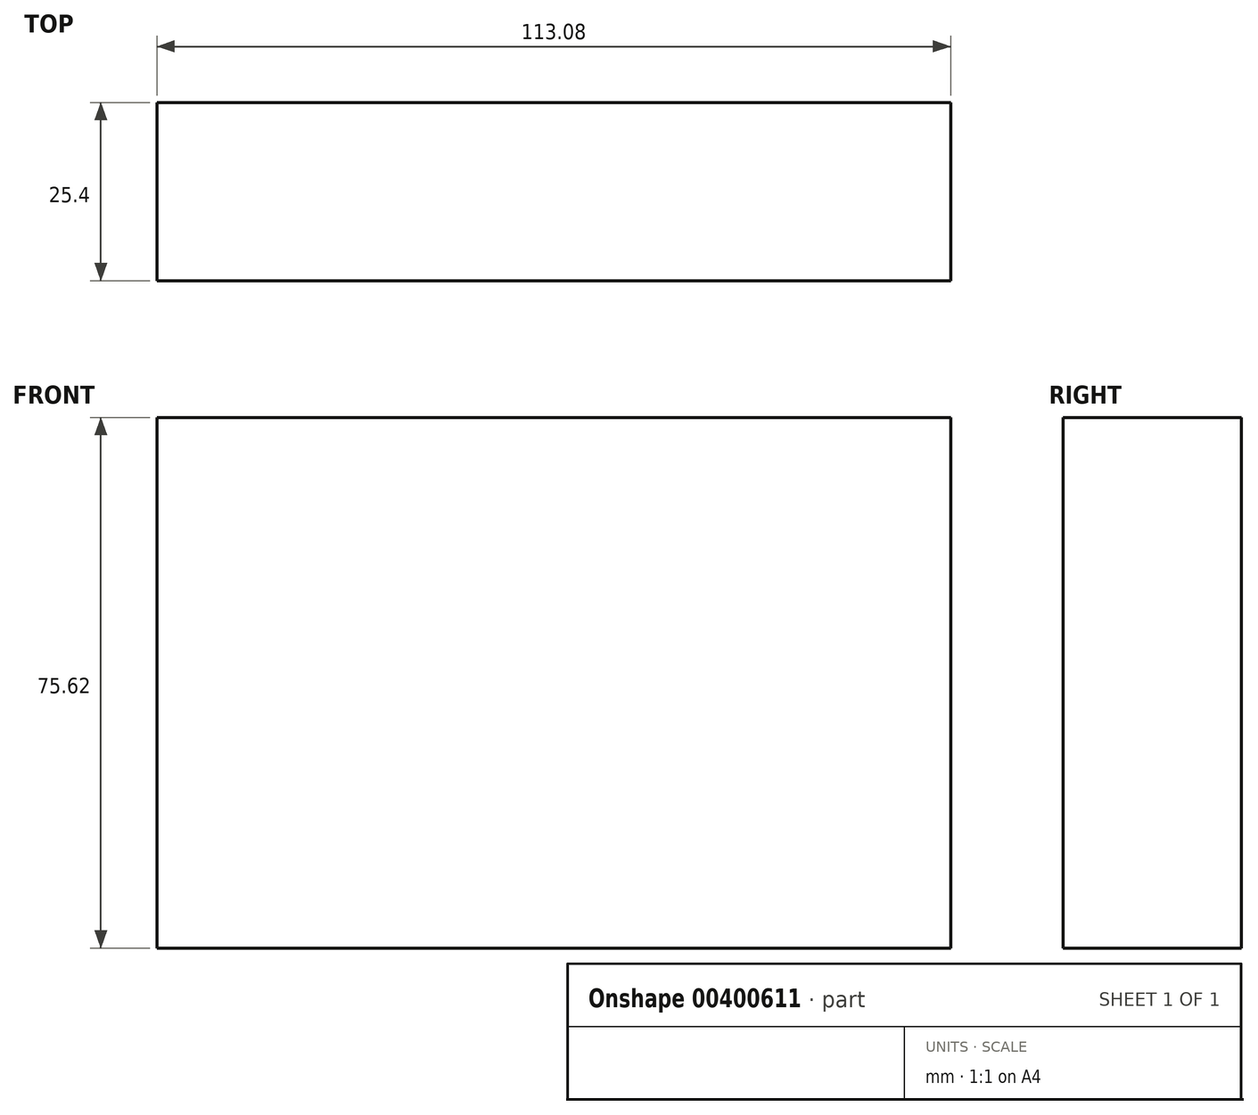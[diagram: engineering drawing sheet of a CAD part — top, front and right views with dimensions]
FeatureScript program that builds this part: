
annotation { "Feature Type Name" : "Feature", "Feature Type Description" : "" }
export const myFeature = defineFeature(function(context is Context, id is Id, definition is map)
    precondition{}
    {
        {
            var Q0;
            Q0=qCreatedBy(makeId("Front.planeOp"),FACE);
            var sketch = newSketch(context, id + "F0", { "sketchPlane" : qUnion([Q0])});
            skLineSegment(sketch, "E0.bottom", {"start": v(0, 0) * mm, "end": v(113.08, 0) * mm});
            skLineSegment(sketch, "E0.top", {"start": v(0, -75.62) * mm, "end": v(113.08, -75.62) * mm});
            skLineSegment(sketch, "E0.left", {"start": v(0, 0) * mm, "end": v(0, -75.62) * mm});
            skLineSegment(sketch, "E0.right", {"start": v(113.08, 0) * mm, "end": v(113.08, -75.62) * mm});
            skSolve(sketch);
        }
        {
            var Q0;
            Q0 = qSketchRegion(id + "F0", true);
            extrude(context, id + "F1", {"entities" : qUnion([Q0]), "depth" : 25.4 * mm});
        }
    });
